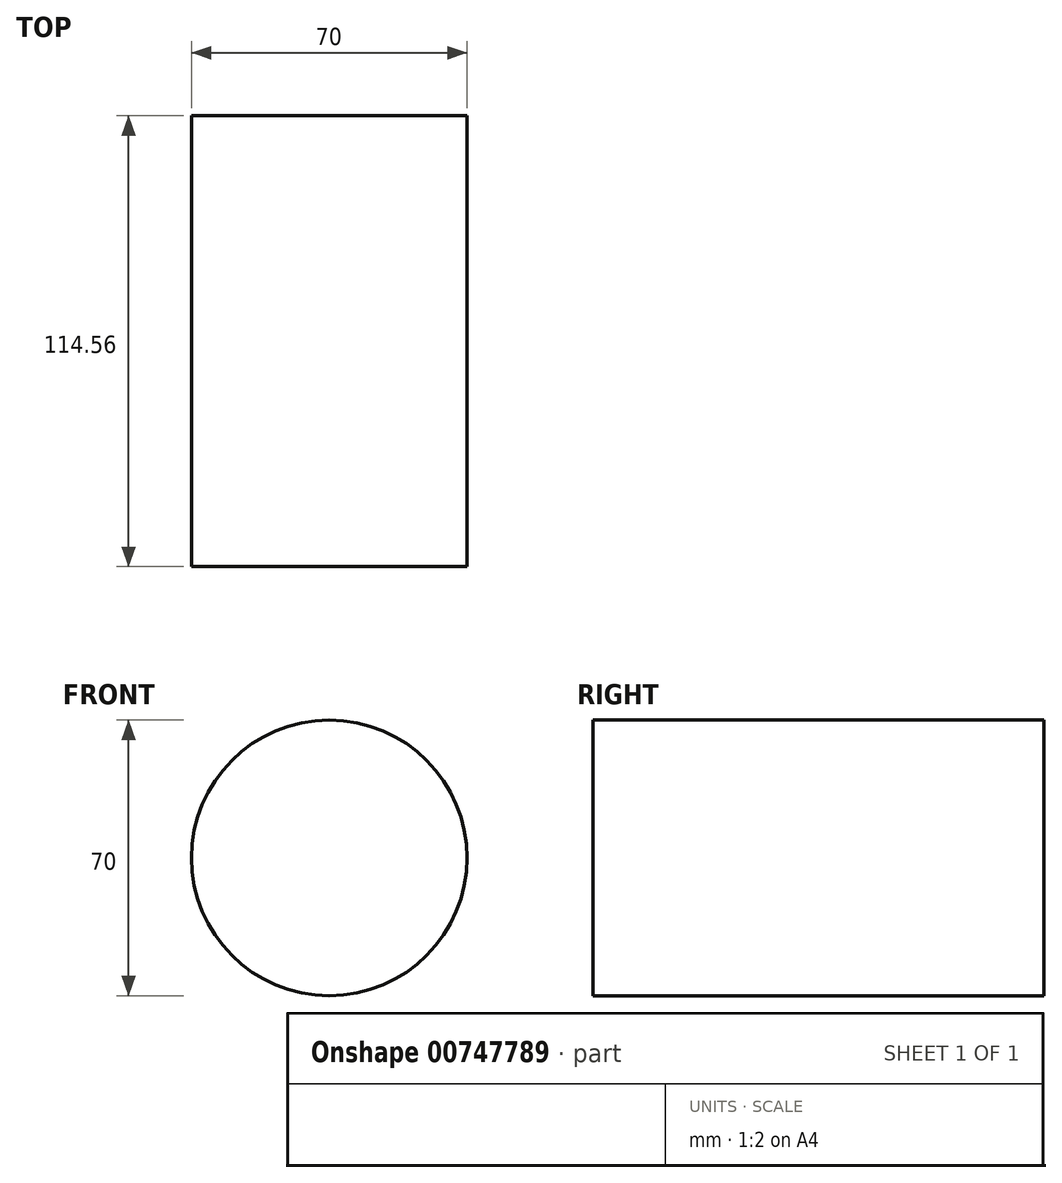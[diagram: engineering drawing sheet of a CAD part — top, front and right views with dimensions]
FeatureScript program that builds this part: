
annotation { "Feature Type Name" : "Feature", "Feature Type Description" : "" }
export const myFeature = defineFeature(function(context is Context, id is Id, definition is map)
    precondition{}
    {
        {
            var Q0;
            Q0=qCreatedBy(makeId("Front.planeOp"),FACE);
            var sketch = newSketch(context, id + "F0", { "sketchPlane" : qUnion([Q0])});
            skCircle(sketch, "E0", {"center": v(0, 0) * mm, "radius": 35 * mm});
            skSolve(sketch);
        }
        {
            var Q0;
            Q0=makeQuery(id+"F0.imprint","IMPRINT",FACE,{"disambiguationData":[TD([[makeQuery(id+"F0.imprint","IMPRINT",EDGE,{"derivedFrom":sQuery(id+"F0.wireOp",EDGE,"E0")}),1.0]])]});
            extrude(context, id + "F1", {"entities" : qUnion([Q0]), "endBound" : BoundingType.SYMMETRIC, "depth" : 114.55 * mm, "offsetDistance" : 25.4 * mm});
        }
    });
